# Revit family: 4595
name_source: partatom
category: Plumbing Fixtures
units: mm (PartAtom-declared; Revit-internal decimal feet)

## family parameters
Always vertical = Yes
Cut with Voids When Loaded = No
OmniClass Number = 23.45.00.00
OmniClass Title = Sanitary, Laundry, and Cleaning Equipment
Part Type = Normal
Room Calculation Point = No
Round Connector Dimension = Use Diameter
Shared = No
Work Plane-Based = No

## types (1)
- 305x787x1016mm
    Activation by = Mechanical Front Bubbler Button
    Approx. Shipping Weigh = 225 lbs
    Assembly Code = D2010810
    Bubbler Style = Vandal Resistant
    CW Connection = Yes
    Chilling Option = Non-refrigerated
    Description = 4595, STONE FTN, ADA, BI-LVL, PDSTL
    Dimensions (L x W x H) = 12 inch x 31 inch x 38 1/ 2inch
    Drain_Outlet = 32 mm  [stored 0.104987 ft]
    Finish = Stone Aggregate
    HW Connection = No
    Installation Location = Outdoor
    Manufacturer = Elkay
    Model = 4595
    Mounting Type = Floor Mount/Freestanding
    No. of Stations Served = 2
    Power = No Electrical Required
    URL = http://www.elkay.com
    Vent Connection = Yes
    Version = 1.0.0.0
    Waste Connection = No
    Water_Inlet = 10 mm  [stored 0.0328084 ft]

note: [stored X ft] marks values corroborated as IEEE doubles in the binary element streams (Revit-internal decimal feet)

## geometry (parser evidence)
native form markers: Sweep x14
no freeform markers — native parametric forms only
